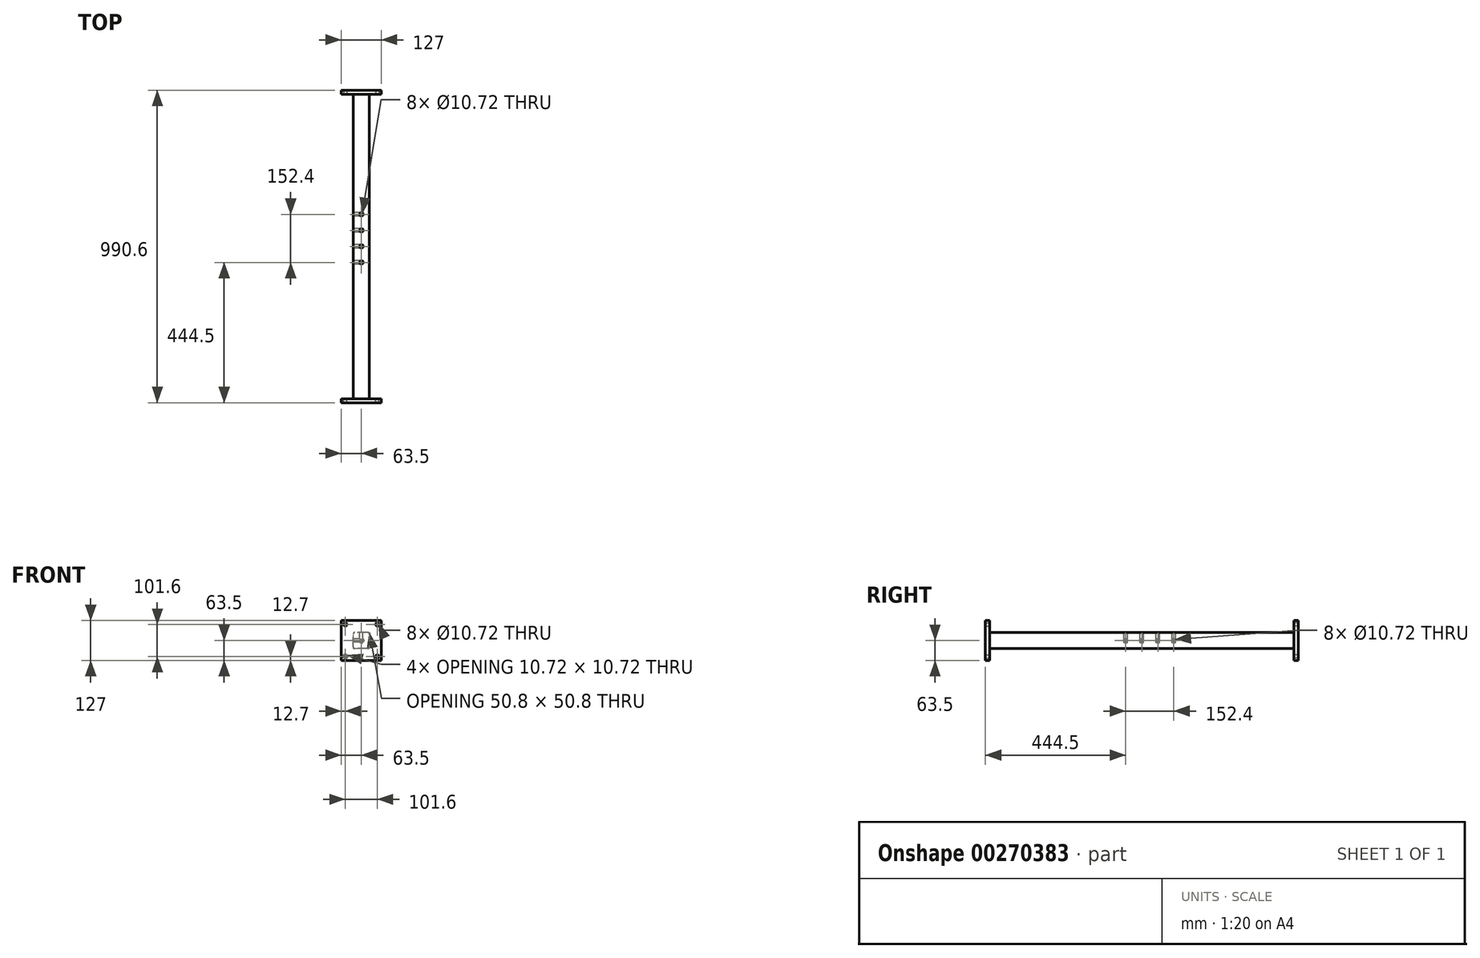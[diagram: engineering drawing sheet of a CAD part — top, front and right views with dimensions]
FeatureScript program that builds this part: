
annotation { "Feature Type Name" : "Feature", "Feature Type Description" : "" }
export const myFeature = defineFeature(function(context is Context, id is Id, definition is map)
    precondition{}
    {
        {
            var Q0;
            Q0=qCreatedBy(makeId("Front.planeOp"),FACE);
            var sketch = newSketch(context, id + "F0", { "sketchPlane" : qUnion([Q0])});
            skLineSegment(sketch, "E0.bottom", {"start": v(25.4, -25.4) * mm, "end": v(-25.4, -25.4) * mm});
            skLineSegment(sketch, "E0.top", {"start": v(25.4, 25.4) * mm, "end": v(-25.4, 25.4) * mm});
            skLineSegment(sketch, "E0.left", {"start": v(25.4, -25.4) * mm, "end": v(25.4, 25.4) * mm});
            skLineSegment(sketch, "E0.right", {"start": v(-25.4, -25.4) * mm, "end": v(-25.4, 25.4) * mm});
            skPoint(sketch, "E0.middle", {"position": v(0, 0) * mm});
            skSolve(sketch);
        }
        {
            var Q0;
            Q0=makeQuery(id+"F0.imprint","IMPRINT",FACE,{"disambiguationData":[TD([[makeQuery(id+"F0.imprint","IMPRINT",EDGE,{"derivedFrom":sQuery(id+"F0.wireOp",EDGE,"E0.bottom")}),-1.0]])]});
            extrude(context, id + "F1", {"entities" : qUnion([Q0]), "endBound" : BoundingType.SYMMETRIC, "depth" : 965.2 * mm});
        }
        {
            var Q0;
            Q0=makeQuery(id+"F1.opExtrude","CAP_FACE",FACE,{"disambiguationData":[OSD([sQuery(id+"F0.wireOp",EDGE,"E0.bottom"),sQuery(id+"F0.wireOp",EDGE,"E0.top"),sQuery(id+"F0.wireOp",EDGE,"E0.left"),sQuery(id+"F0.wireOp",EDGE,"E0.right")])],"isStart":false});
            var sketch = newSketch(context, id + "F2", { "sketchPlane" : qUnion([Q0])});
            skLineSegment(sketch, "E1.bottom", {"start": v(-63.5, 63.5) * mm, "end": v(63.5, 63.5) * mm});
            skLineSegment(sketch, "E1.top", {"start": v(-63.5, -63.5) * mm, "end": v(63.5, -63.5) * mm});
            skLineSegment(sketch, "E1.left", {"start": v(-63.5, 63.5) * mm, "end": v(-63.5, -63.5) * mm});
            skLineSegment(sketch, "E1.right", {"start": v(63.5, 63.5) * mm, "end": v(63.5, -63.5) * mm});
            skPoint(sketch, "E1.middle", {"position": v(0, 0) * mm});
            skPoint(sketch, "E2", {"position": v(-50.8, 50.8) * mm});
            skPoint(sketch, "E3", {"position": v(50.8, 50.8) * mm});
            skPoint(sketch, "E4.MirrorP", {"position": v(-50.8, -50.8) * mm});
            skPoint(sketch, "E5.MirrorP", {"position": v(50.8, -50.8) * mm});
            skSolve(sketch);
        }
        {
            var Q0;
            {var subQ2=sQuery(id+"F2.wireOp",EDGE,"E1.left");Q0=makeQuery(id+"F2.imprint","IMPRINT",FACE,{"disambiguationData":[TD([[makeQuery(id+"F2.imprint","IMPRINT",EDGE,{"derivedFrom":subQ2}),1.0]])]});}
            var Q1;
            {var subQ1=makeQuery(id+"F1.opExtrude","CAP_EDGE",EDGE,{"disambiguationData":[OSD([sQuery(id+"F0.wireOp",EDGE,"E0.left")])],"isStart":false});Q1=makeQuery(id+"F2.imprint","IMPRINT",FACE,{"disambiguationData":[TD([[makeQuery(id+"F2.imprint","IMPRINT",EDGE,{"derivedFrom":subQ1}),1.0]])]});}
            var Q2;
            {var subQ2=sQuery(id+"F2.wireOp",EDGE,"E1.right");Q2=makeQuery(id+"F2.imprint","IMPRINT",FACE,{"disambiguationData":[TD([[makeQuery(id+"F2.imprint","IMPRINT",EDGE,{"derivedFrom":subQ2}),-1.0]])]});}
            extrude(context, id + "F3", {"entities" : qUnion([Q0, Q1, Q2]), "operationType" : NewBodyOperationType.ADD, "depth" : 12.7 * mm});
        }
        {
            var Q0;
            Q0=makeQuery(id+"F1.opExtrude","SWEPT_EDGE",EDGE,{"disambiguationData":[OSD([sQuery(id+"F0.wireOp",EDGE,"E0.top"),sQuery(id+"F0.wireOp",EDGE,"E0.left")])]});
            var Q1;
            Q1=makeQuery(id+"F1.opExtrude","SWEPT_EDGE",EDGE,{"disambiguationData":[OSD([sQuery(id+"F0.wireOp",EDGE,"E0.top"),sQuery(id+"F0.wireOp",EDGE,"E0.right")])]});
            var Q2;
            Q2=makeQuery(id+"F1.opExtrude","SWEPT_EDGE",EDGE,{"disambiguationData":[OSD([sQuery(id+"F0.wireOp",EDGE,"E0.bottom"),sQuery(id+"F0.wireOp",EDGE,"E0.right")])]});
            var Q3;
            Q3=makeQuery(id+"F1.opExtrude","SWEPT_EDGE",EDGE,{"disambiguationData":[OSD([sQuery(id+"F0.wireOp",EDGE,"E0.bottom"),sQuery(id+"F0.wireOp",EDGE,"E0.left")])]});
            fillet(context, id + "F4", {"entities" : qUnion([Q0, Q1, Q2, Q3]), "radius" : 5.08 * mm, "tangentPropagation" : true, "allowEdgeOverflow" : false});
        }
        {
            var Q0;
            Q0=sQuery(id+"F2.wireOp",VERTEX,"d6c5f8c2-4952-45da-8af8-aec65ad9689a");
            var Q1;
            Q1=sQuery(id+"F2.wireOp",VERTEX,"6a845007-e081-4299-b110-cdbb86e047b90.MirrorP");
            var Q2;
            Q2=sQuery(id+"F2.wireOp",VERTEX,"616deb48-94fe-4589-9c3d-a1012ffcebe7");
            var Q3;
            Q3=sQuery(id+"F2.wireOp",VERTEX,"479cd291-fab3-4c9f-a41b-5b79fb7b620f0.MirrorP");
            var Q4;
            Q4=sQuery(id+"F2.wireOp",VERTEX,"E2");
            var Q5;
            Q5=sQuery(id+"F2.wireOp",VERTEX,"E3");
            var Q6;
            Q6=sQuery(id+"F2.wireOp",VERTEX,"E5.MirrorP");
            var Q7;
            Q7=sQuery(id+"F2.wireOp",VERTEX,"E4.MirrorP");
            var Q8;
            Q8=makeQuery(id+"F1.opExtrude","SWEPT_BODY",BODY,{"disambiguationData":[OSD([sQuery(id+"F0.wireOp",EDGE,"E0.bottom"),sQuery(id+"F0.wireOp",EDGE,"E0.top"),sQuery(id+"F0.wireOp",EDGE,"E0.left"),sQuery(id+"F0.wireOp",EDGE,"E0.right")])]});
            hole(context, id + "F5", {"style" : HoleStyle.SIMPLE, "endStyle" : HoleEndStyle.THROUGH, "oppositeDirection" : true, "standardTappedOrClearance" : lookupTablePath({ "standard" : "ANSI", "engagement" : "75%", "pitch" : "13 tpi", "size" : "1/2", "type" : "Tapped" }), "standardBlindInLast" : lookupTablePath({ "standard" : "ANSI", "engagement" : "75%", "pitch" : "13 tpi", "size" : "1/2", "type" : "Tapped" }), "holeDiameter" : 10.72 * mm, "showTappedDepth" : true, "tappedDepth" : 12.7 * mm, "tapClearance" : 3, "startFromSketch" : true, "locations" : qUnion([Q0, Q1, Q2, Q3, Q4, Q5, Q6, Q7]), "scope" : qUnion([Q8]), "majorDiameter" : 12.7 * mm});
        }
        {
            var Q0;
            Q0=makeQuery(id+"F1.opExtrude","SWEPT_BODY",BODY,{"disambiguationData":[OSD([sQuery(id+"F0.wireOp",EDGE,"E0.bottom"),sQuery(id+"F0.wireOp",EDGE,"E0.top"),sQuery(id+"F0.wireOp",EDGE,"E0.left"),sQuery(id+"F0.wireOp",EDGE,"E0.right")])]});
            var Q1;
            Q1=qCreatedBy(makeId("Front.planeOp"),FACE);
            mirror(context, id + "F6", {"operationType" : NewBodyOperationType.ADD, "entities" : qUnion([Q0]), "mirrorPlane" : qUnion([Q1])});
        }
        {
            var Q0;
            Q0=makeQuery(id+"F1.opExtrude","SWEPT_FACE",FACE,{"disambiguationData":[OSD([sQuery(id+"F0.wireOp",EDGE,"E0.right")])]});
            var sketch = newSketch(context, id + "F7", { "sketchPlane" : qUnion([Q0])});
            skPoint(sketch, "E6", {"position": v(-50.8, 0) * mm});
            skPoint(sketch, "E7.MirrorP", {"position": v(50.8, 0) * mm});
            skPoint(sketch, "E8", {"position": v(-101.6, 0) * mm});
            skPoint(sketch, "E9", {"position": v(0, 0) * mm});
            skSolve(sketch);
        }
        {
            var Q0;
            Q0=makeQuery(id+"F1.opExtrude","SWEPT_FACE",FACE,{"disambiguationData":[OSD([sQuery(id+"F0.wireOp",EDGE,"E0.top")])]});
            var sketch = newSketch(context, id + "F8", { "sketchPlane" : qUnion([Q0])});
            skPoint(sketch, "E10", {"position": v(0, 0) * mm});
            skPoint(sketch, "E11", {"position": v(0, 101.6) * mm});
            skPoint(sketch, "E12", {"position": v(0, 50.8) * mm});
            skPoint(sketch, "E13", {"position": v(0, -50.8) * mm});
            skSolve(sketch);
        }
        {
            var Q0;
            Q0=sQuery(id+"F7.wireOp",VERTEX,"E6");
            var Q1;
            Q1=sQuery(id+"F7.wireOp",VERTEX,"E7.MirrorP");
            var Q2;
            Q2=sQuery(id+"F8.wireOp",VERTEX,"E10");
            var Q3;
            Q3=sQuery(id+"F8.wireOp",VERTEX,"E11");
            var Q4;
            Q4=sQuery(id+"F7.wireOp",VERTEX,"E8");
            var Q5;
            Q5=sQuery(id+"F7.wireOp",VERTEX,"E9");
            var Q6;
            Q6=sQuery(id+"F8.wireOp",VERTEX,"E12");
            var Q7;
            Q7=sQuery(id+"F8.wireOp",VERTEX,"E13");
            var Q8;
            Q8=makeQuery(id+"F1.opExtrude","SWEPT_BODY",BODY,{"disambiguationData":[OSD([sQuery(id+"F0.wireOp",EDGE,"E0.bottom"),sQuery(id+"F0.wireOp",EDGE,"E0.top"),sQuery(id+"F0.wireOp",EDGE,"E0.left"),sQuery(id+"F0.wireOp",EDGE,"E0.right")])]});
            hole(context, id + "F9", {"style" : HoleStyle.SIMPLE, "endStyle" : HoleEndStyle.BLIND, "standardTappedOrClearance" : lookupTablePath({ "standard" : "ANSI", "engagement" : "75%", "pitch" : "13 tpi", "size" : "1/2", "type" : "Tapped" }), "standardBlindInLast" : lookupTablePath({ "standard" : "ANSI", "engagement" : "75%", "pitch" : "13 tpi", "size" : "1/2", "type" : "Tapped" }), "holeDiameter" : 10.72 * mm, "showTappedDepth" : true, "holeDepth" : 31.26 * mm, "tappedDepth" : 25.4 * mm, "tapClearance" : 3, "startFromSketch" : true, "locations" : qUnion([Q0, Q1, Q2, Q3, Q4, Q5, Q6, Q7]), "scope" : qUnion([Q8]), "majorDiameter" : 12.7 * mm});
        }
    });
